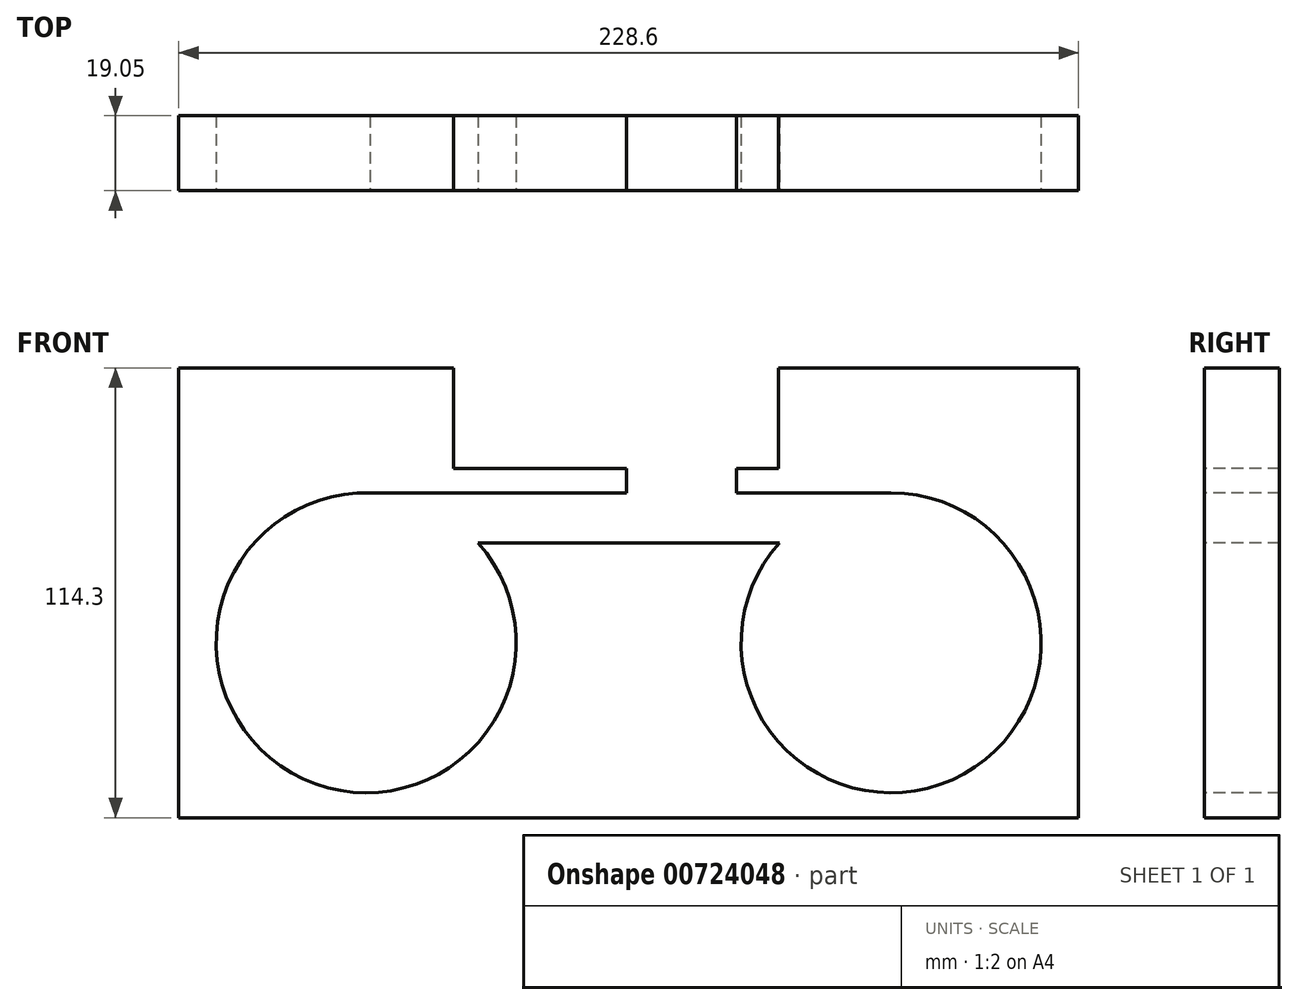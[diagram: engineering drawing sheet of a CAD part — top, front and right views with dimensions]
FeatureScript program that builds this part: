
annotation { "Feature Type Name" : "Feature", "Feature Type Description" : "" }
export const myFeature = defineFeature(function(context is Context, id is Id, definition is map)
    precondition{}
    {
        {
            var Q0;
            Q0=qCreatedBy(makeId("Front.planeOp"),FACE);
            var sketch = newSketch(context, id + "F0", { "sketchPlane" : qUnion([Q0])});
            skLineSegment(sketch, "E0.bottom", {"start": v(0, 0) * mm, "end": v(228.6, 0) * mm});
            skLineSegment(sketch, "E0.top", {"start": v(0, 114.3) * mm, "end": v(228.6, 114.3) * mm});
            skLineSegment(sketch, "E0.left", {"start": v(0, 0) * mm, "end": v(0, 114.3) * mm});
            skLineSegment(sketch, "E0.right", {"start": v(228.6, 0) * mm, "end": v(228.6, 114.3) * mm});
            skSolve(sketch);
        }
        {
            var Q0;
            Q0=makeQuery(id+"F0.imprint","IMPRINT",FACE,{"disambiguationData":[TD([[makeQuery(id+"F0.imprint","IMPRINT",EDGE,{"derivedFrom":sQuery(id+"F0.wireOp",EDGE,"E0.bottom")}),1.0]])]});
            extrude(context, id + "F1", {"entities" : qUnion([Q0]), "depth" : 19.05 * mm, "offsetDistance" : 25.4 * mm});
        }
        {
            var Q0;
            Q0=makeQuery(id+"F1.opExtrude","CAP_FACE",FACE,{"disambiguationData":[OSD([sQuery(id+"F0.wireOp",EDGE,"E0.bottom"),sQuery(id+"F0.wireOp",EDGE,"E0.top"),sQuery(id+"F0.wireOp",EDGE,"E0.left"),sQuery(id+"F0.wireOp",EDGE,"E0.right")])],"isStart":false});
            var sketch = newSketch(context, id + "F2", { "sketchPlane" : qUnion([Q0])});
            skCircle(sketch, "E1", {"center": v(47.63, 44.45) * mm, "radius": 38.1 * mm});
            skCircle(sketch, "E2", {"center": v(180.97, 44.45) * mm, "radius": 38.1 * mm});
            skSolve(sketch);
        }
        {
            var Q0;
            Q0=makeQuery(id+"F2.imprint","IMPRINT",FACE,{"disambiguationData":[TD([[makeQuery(id+"F2.imprint","IMPRINT",EDGE,{"derivedFrom":sQuery(id+"F2.wireOp",EDGE,"E1")}),1.0]])]});
            var Q1;
            Q1=makeQuery(id+"F2.imprint","IMPRINT",FACE,{"disambiguationData":[TD([[makeQuery(id+"F2.imprint","IMPRINT",EDGE,{"derivedFrom":sQuery(id+"F2.wireOp",EDGE,"E2")}),1.0]])]});
            extrude(context, id + "F3", {"entities" : qUnion([Q0, Q1]), "operationType" : NewBodyOperationType.REMOVE, "oppositeDirection" : true, "depth" : 25.4 * mm, "offsetDistance" : 25.4 * mm});
        }
        {
            var Q0;
            Q0=makeQuery(id+"F1.opExtrude","CAP_FACE",FACE,{"disambiguationData":[OSD([sQuery(id+"F0.wireOp",EDGE,"E0.bottom"),sQuery(id+"F0.wireOp",EDGE,"E0.top"),sQuery(id+"F0.wireOp",EDGE,"E0.left"),sQuery(id+"F0.wireOp",EDGE,"E0.right")])],"isStart":false});
            var sketch = newSketch(context, id + "F4", { "sketchPlane" : qUnion([Q0])});
            skLineSegment(sketch, "E3", {"start": v(180.97, 82.55) * mm, "end": v(152.57, 69.84) * mm});
            skLineSegment(sketch, "E4", {"start": v(152.57, 69.84) * mm, "end": v(76.03, 69.84) * mm});
            skLineSegment(sketch, "E5", {"start": v(76.03, 69.84) * mm, "end": v(46.62, 82.54) * mm});
            skLineSegment(sketch, "E6", {"start": v(69.85, 114.3) * mm, "end": v(69.85, 88.72) * mm});
            skLineSegment(sketch, "E7", {"start": v(152.4, 88.73) * mm, "end": v(152.4, 114.3) * mm});
            skLineSegment(sketch, "E8", {"start": v(152.4, 114.3) * mm, "end": v(69.85, 114.3) * mm});
            skLineSegment(sketch, "E9", {"start": v(141.67, 88.72) * mm, "end": v(141.67, 82.55) * mm});
            skLineSegment(sketch, "E10", {"start": v(113.8, 82.54) * mm, "end": v(113.8, 88.72) * mm});
            skLineSegment(sketch, "E11", {"start": v(46.62, 82.54) * mm, "end": v(113.8, 82.54) * mm});
            skLineSegment(sketch, "E12", {"start": v(180.97, 82.55) * mm, "end": v(141.67, 82.55) * mm});
            skLineSegment(sketch, "E13", {"start": v(152.4, 88.73) * mm, "end": v(141.67, 88.72) * mm});
            skLineSegment(sketch, "E14", {"start": v(113.8, 88.72) * mm, "end": v(69.85, 88.72) * mm});
            skSolve(sketch);
        }
        {
            var Q0;
            {var subQ5=sQuery(id+"F4.wireOp",EDGE,"E4");Q0=makeQuery(id+"F4.imprint","IMPRINT",FACE,{"disambiguationData":[TD([[makeQuery(id+"F4.imprint","IMPRINT",EDGE,{"derivedFrom":subQ5}),-1.0]])]});}
            extrude(context, id + "F5", {"entities" : qUnion([Q0]), "operationType" : NewBodyOperationType.REMOVE, "oppositeDirection" : true, "depth" : 25.4 * mm, "offsetDistance" : 25.4 * mm});
        }
    });
